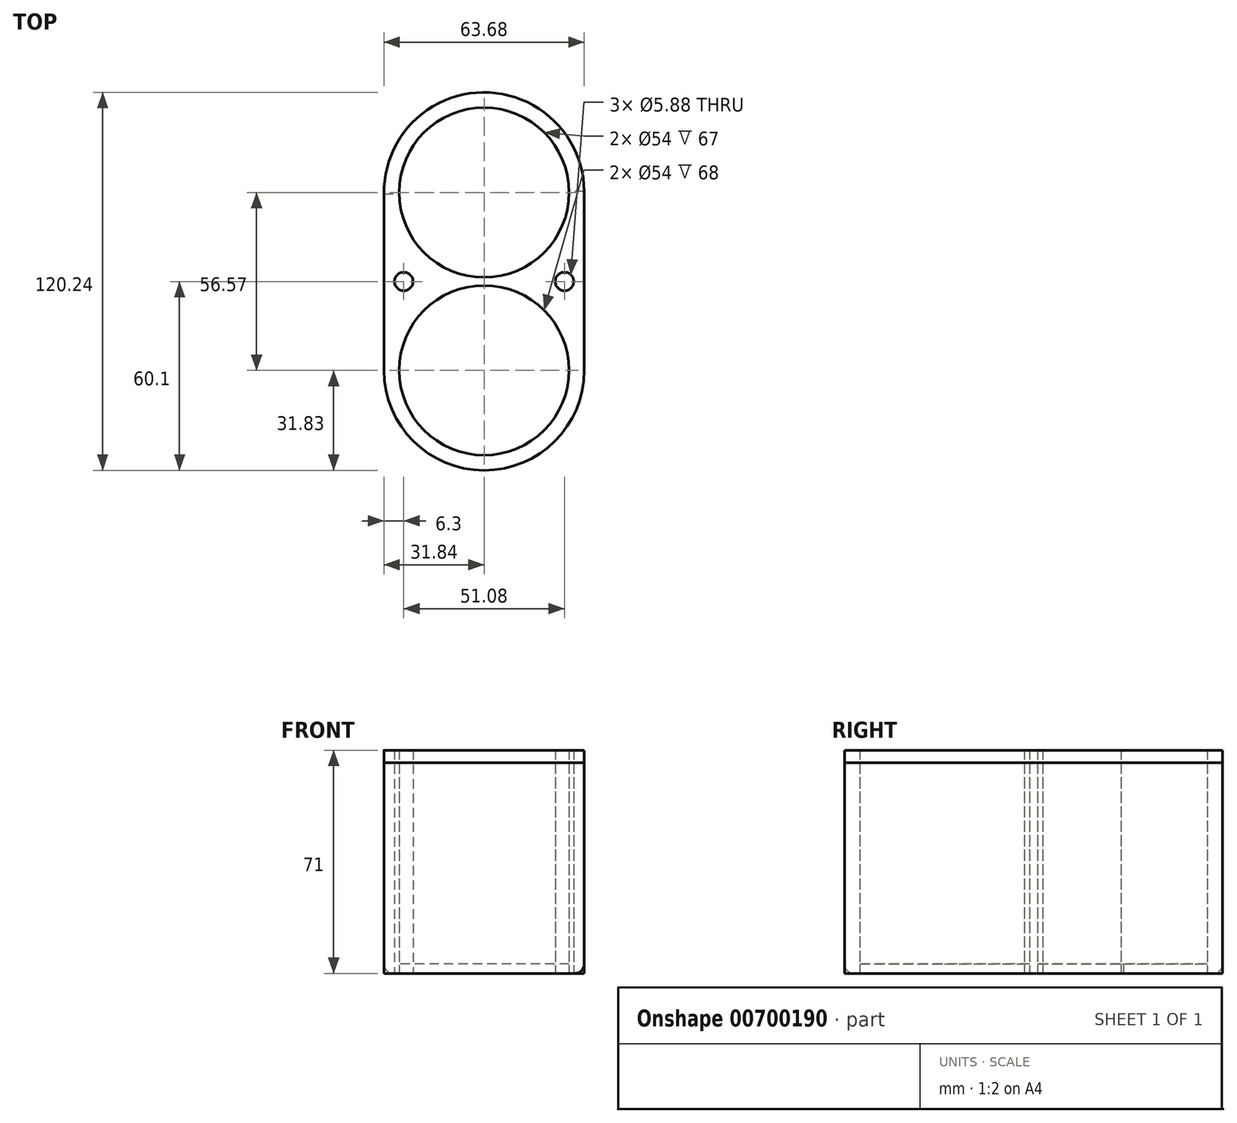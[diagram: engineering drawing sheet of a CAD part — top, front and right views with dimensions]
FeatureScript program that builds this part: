
annotation { "Feature Type Name" : "Feature", "Feature Type Description" : "" }
export const myFeature = defineFeature(function(context is Context, id is Id, definition is map)
    precondition{}
    {
        {
            var Q0;
            Q0=qCreatedBy(makeId("Top.planeOp"),FACE);
            var sketch = newSketch(context, id + "F0", { "sketchPlane" : qUnion([Q0])});
            skCircle(sketch, "E0", {"center": v(0, -28.27) * mm, "radius": 27 * mm});
            skCircle(sketch, "E1", {"center": v(0, 28.3) * mm, "radius": 27 * mm});
            skArc(sketch, "E2", {"start": v(31.84, 27.98) * mm, "mid": v(-0.07, 60.14) * mm, "end": v(-31.84, 27.83) * mm});
            skArc(sketch, "E3", {"start": v(-31.84, -28.26) * mm, "mid": v(0, -60.1) * mm, "end": v(31.84, -28.27) * mm});
            skLineSegment(sketch, "E4", {"start": v(-31.84, 27.83) * mm, "end": v(-31.84, -28.26) * mm});
            skLineSegment(sketch, "E5", {"start": v(31.84, 27.98) * mm, "end": v(31.84, -28.27) * mm});
            skLineSegment(sketch, "E6.left", {"start": v(25.54, 0) * mm, "end": v(25.54, 0) * mm});
            skLineSegment(sketch, "E6.right", {"start": v(-25.54, 0) * mm, "end": v(-25.54, 0) * mm});
            skPoint(sketch, "E6.middle", {"position": v(0, 0) * mm});
            skCircle(sketch, "E7", {"center": v(-25.54, 0) * mm, "radius": 2.94 * mm});
            skCircle(sketch, "E8.MirrorC", {"center": v(25.54, 0) * mm, "radius": 2.94 * mm});
            skLineSegment(sketch, "E9.bottom", {"start": v(-1.1, 60.12) * mm, "end": v(1.1, 60.12) * mm});
            skLineSegment(sketch, "E9.left", {"start": v(-31.84, 28.71) * mm, "end": v(-31.84, -28.67) * mm});
            skLineSegment(sketch, "E9.right", {"start": v(31.84, 28.71) * mm, "end": v(31.84, -28.67) * mm});
            skPoint(sketch, "E9.top.end.orphan", {"position": v(31.84, -60.12) * mm});
            skPoint(sketch, "E10.orphan", {"position": v(-31.84, -60.12) * mm});
            skPoint(sketch, "E11.orphan", {"position": v(-31.84, 60.12) * mm});
            skPoint(sketch, "E12.orphan", {"position": v(31.84, 60.12) * mm});
            skSolve(sketch);
        }
        {
            var Q0;
            Q0=makeQuery(id+"F0.imprint","IMPRINT",FACE,{"disambiguationData":[TD([[makeQuery(id+"F0.imprint","IMPRINT",EDGE,{"derivedFrom":sQuery(id+"F0.wireOp",EDGE,"E0")}),-1.0]])]});
            var Q1;
            {var subQ3=sQuery(id+"F0.wireOp",EDGE,"E4");Q1=makeQuery(id+"F0.imprint","IMPRINT",FACE,{"disambiguationData":[TD([[makeQuery(id+"F0.imprint","IMPRINT",EDGE,{"derivedFrom":subQ3}),1.0]])]});}
            var Q2;
            {var subQ3=sQuery(id+"F0.wireOp",EDGE,"E5");Q2=makeQuery(id+"F0.imprint","IMPRINT",FACE,{"disambiguationData":[TD([[makeQuery(id+"F0.imprint","IMPRINT",EDGE,{"derivedFrom":subQ3}),-1.0]])]});}
            extrude(context, id + "F1", {"entities" : qUnion([Q0, Q1, Q2]), "depth" : 71 * mm, "offsetDistance" : 25 * mm});
        }
        {
            var Q0;
            Q0 = qSketchRegion(id + "F0", true);
            var Q1;
            Q1=makeQuery(id+"F0.imprint","IMPRINT",FACE,{"disambiguationData":[TD([[makeQuery(id+"F0.imprint","IMPRINT",EDGE,{"derivedFrom":sQuery(id+"F0.wireOp",EDGE,"E1")}),1.0]])]});
            var Q2;
            Q2=makeQuery(id+"F0.imprint","IMPRINT",FACE,{"disambiguationData":[TD([[makeQuery(id+"F0.imprint","IMPRINT",EDGE,{"derivedFrom":sQuery(id+"F0.wireOp",EDGE,"E0")}),1.0]])]});
            var Q3;
            Q3=sQuery(id+"F0.wireOp",EDGE,"E9.left");
            var Q4;
            Q4=sQuery(id+"F0.wireOp",EDGE,"E9.bottom");
            var Q5;
            Q5=sQuery(id+"F0.wireOp",EDGE,"E9.right");
            var Q6;
            Q6=sQuery(id+"F0.wireOp",EDGE,"E9.top");
            extrude(context, id + "F2", {"entities" : qUnion([Q0, Q1, Q2]), "operationType" : NewBodyOperationType.ADD, "surfaceEntities" : qUnion([Q3, Q4, Q5, Q6]), "depth" : 3 * mm, "offsetDistance" : 25 * mm});
        }
        {
            var Q0;
            {var subQ0=sQuery(id+"F0.wireOp",EDGE,"E2");var subQ1=sQuery(id+"F0.wireOp",EDGE,"E9.bottom");Q0=makeQuery(id+"F2.boolean.opBoolean","MERGE",EDGE,{"derivedFrom":[makeQuery(id+"F1.opExtrude","CAP_EDGE",EDGE,{"disambiguationData":[OSD([subQ0]),TDD([makeQuery(id+"F0.imprint","IMPRINT",EDGE,{"disambiguationData":[TD([[makeQuery(id+"F0.imprint","INTERSECT",VERTEX,{"derivedFrom":[subQ0,sQuery(id+"F0.wireOp",EDGE,"E5")]}),-1.0]])],"derivedFrom":subQ0}),makeQuery(id+"F0.imprint","IMPRINT",EDGE,{"disambiguationData":[TD([[makeQuery(id+"F0.imprint","INTERSECT",VERTEX,{"disambiguationData":[OD(1.0)],"derivedFrom":[subQ0,subQ1]}),1.0]])],"derivedFrom":subQ0})])],"isStart":true}),makeQuery(id+"F1.opExtrude","CAP_EDGE",EDGE,{"disambiguationData":[OSD([subQ0]),TDD([makeQuery(id+"F0.imprint","IMPRINT",EDGE,{"disambiguationData":[TD([[makeQuery(id+"F0.imprint","INTERSECT",VERTEX,{"disambiguationData":[OD(0.0)],"derivedFrom":[subQ0,subQ1]}),-1.0]])],"derivedFrom":subQ0})])],"isStart":true}),makeQuery(id+"F2.opExtrude","CAP_EDGE",EDGE,{"disambiguationData":[OSD([subQ0])],"isStart":true})]});}
            var Q1;
            Q1=makeQuery(id+"F1.opExtrude","CAP_EDGE",EDGE,{"disambiguationData":[OSD([sQuery(id+"F0.wireOp",EDGE,"E3")])],"isStart":true});
            fillet(context, id + "F3", {"entities" : qUnion([Q0, Q1]), "radius" : 3 * mm, "tangentPropagation" : true, "allowEdgeOverflow" : false});
        }
        {
            var Q0;
            Q0=makeQuery(id+"F0.imprint","IMPRINT",FACE,{"disambiguationData":[TD([[makeQuery(id+"F0.imprint","IMPRINT",EDGE,{"derivedFrom":sQuery(id+"F0.wireOp",EDGE,"E7")}),1.0]])]});
            var Q1;
            Q1=makeQuery(id+"F0.imprint","IMPRINT",FACE,{"disambiguationData":[TD([[makeQuery(id+"F0.imprint","IMPRINT",EDGE,{"derivedFrom":sQuery(id+"F0.wireOp",EDGE,"E8.MirrorC")}),-1.0]])]});
            var Q2;
            Q2=sQuery(id+"F0.wireOp",EDGE,"E8.MirrorC");
            var Q3;
            Q3=sQuery(id+"F0.wireOp",EDGE,"E7");
            extrude(context, id + "F4", {"entities" : qUnion([Q0, Q1]), "surfaceEntities" : qUnion([Q2, Q3]), "depth" : 67 * mm, "offsetDistance" : 25 * mm});
        }
    });
